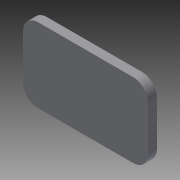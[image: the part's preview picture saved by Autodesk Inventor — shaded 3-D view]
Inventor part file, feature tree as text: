
AUTODESK INVENTOR PART (.ipt)
format: ipt  version: 2013 SP1 (Build 170176100, 176)  size: 78,848 bytes
history: native  units: mm
features: extrude x1, sketch x1
ambient origin geometry x8: Origin, YZ Plane, XZ Plane, XY Plane, X Axis, Y Axis, Z Axis, Center Point
bodies: Solid1 (feature_tree)
feature tree (2):
  extrude  "Extrusion1"  Depth=42.0mm
  sketch  "Sketch1"  dims[d0=5.0mm d1=42.0mm d2=25.0mm d3=5.0mm d4=5.0mm d5=3.0mm d6=0.0mm]
